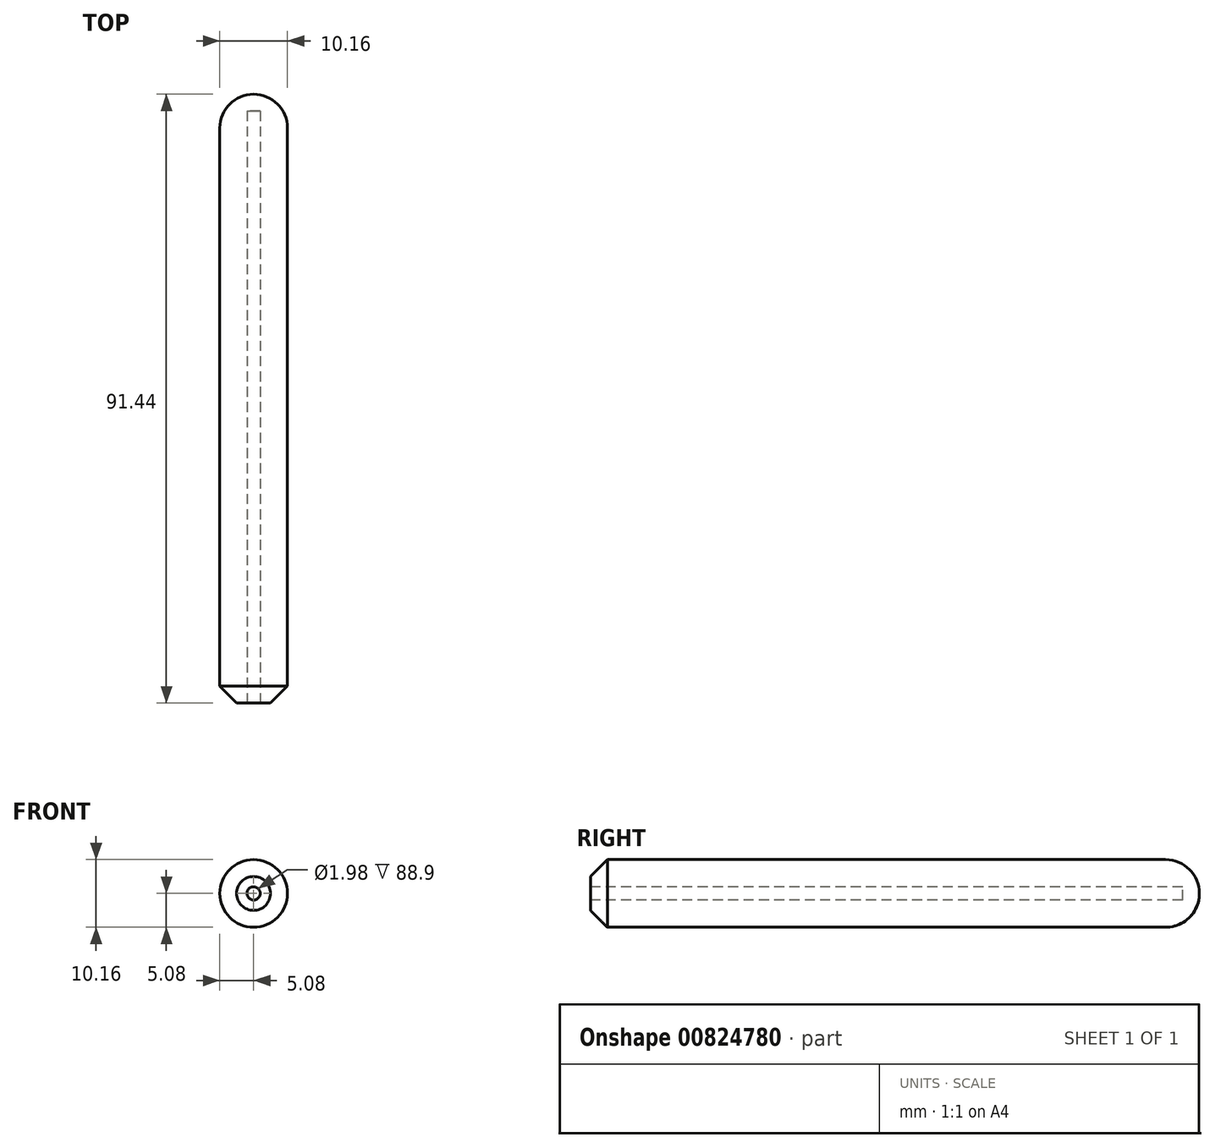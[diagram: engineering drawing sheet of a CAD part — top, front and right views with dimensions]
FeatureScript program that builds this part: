
annotation { "Feature Type Name" : "Feature", "Feature Type Description" : "" }
export const myFeature = defineFeature(function(context is Context, id is Id, definition is map)
    precondition{}
    {
        {
            var Q0;
            Q0=qCreatedBy(makeId("Front.planeOp"),FACE);
            var sketch = newSketch(context, id + "F0", { "sketchPlane" : qUnion([Q0])});
            skCircle(sketch, "E0", {"center": v(0, 0) * mm, "radius": 5.08 * mm});
            skSolve(sketch);
        }
        {
            var Q0;
            Q0=makeQuery(id+"F0.imprint","IMPRINT",FACE,{"disambiguationData":[TD([[makeQuery(id+"F0.imprint","IMPRINT",EDGE,{"derivedFrom":sQuery(id+"F0.wireOp",EDGE,"E0")}),1.0]])]});
            extrude(context, id + "F1", {"entities" : qUnion([Q0]), "depth" : 91.44 * mm, "offsetDistance" : 25.4 * mm});
        }
        {
            var Q0;
            Q0=makeQuery(id+"F1.opExtrude","CAP_FACE",FACE,{"disambiguationData":[OSD([sQuery(id+"F0.wireOp",EDGE,"E0")])],"isStart":false});
            var sketch = newSketch(context, id + "F2", { "sketchPlane" : qUnion([Q0])});
            skCircle(sketch, "E1", {"center": v(0, 0) * mm, "radius": 0.99 * mm});
            skSolve(sketch);
        }
        {
            var Q0;
            Q0=makeQuery(id+"F2.imprint","IMPRINT",FACE,{"disambiguationData":[TD([[makeQuery(id+"F2.imprint","IMPRINT",EDGE,{"derivedFrom":sQuery(id+"F2.wireOp",EDGE,"E1")}),1.0]])]});
            extrude(context, id + "F3", {"entities" : qUnion([Q0]), "operationType" : NewBodyOperationType.REMOVE, "oppositeDirection" : true, "depth" : 88.9 * mm, "offsetDistance" : 25.4 * mm});
        }
        {
            var Q0;
            Q0=makeQuery(id+"F1.opExtrude","CAP_EDGE",EDGE,{"disambiguationData":[OSD([sQuery(id+"F0.wireOp",EDGE,"E0")])],"isStart":false});
            chamfer(context, id + "F4", {"entities" : qUnion([Q0]), "width" : 2.54 * mm, "tangentPropagation" : true});
        }
        {
            var Q0;
            Q0=makeQuery(id+"F1.opExtrude","CAP_EDGE",EDGE,{"disambiguationData":[OSD([sQuery(id+"F0.wireOp",EDGE,"E0")])],"isStart":true});
            fillet(context, id + "F5", {"entities" : qUnion([Q0]), "radius" : 5.08 * mm, "tangentPropagation" : true, "allowEdgeOverflow" : false});
        }
    });
